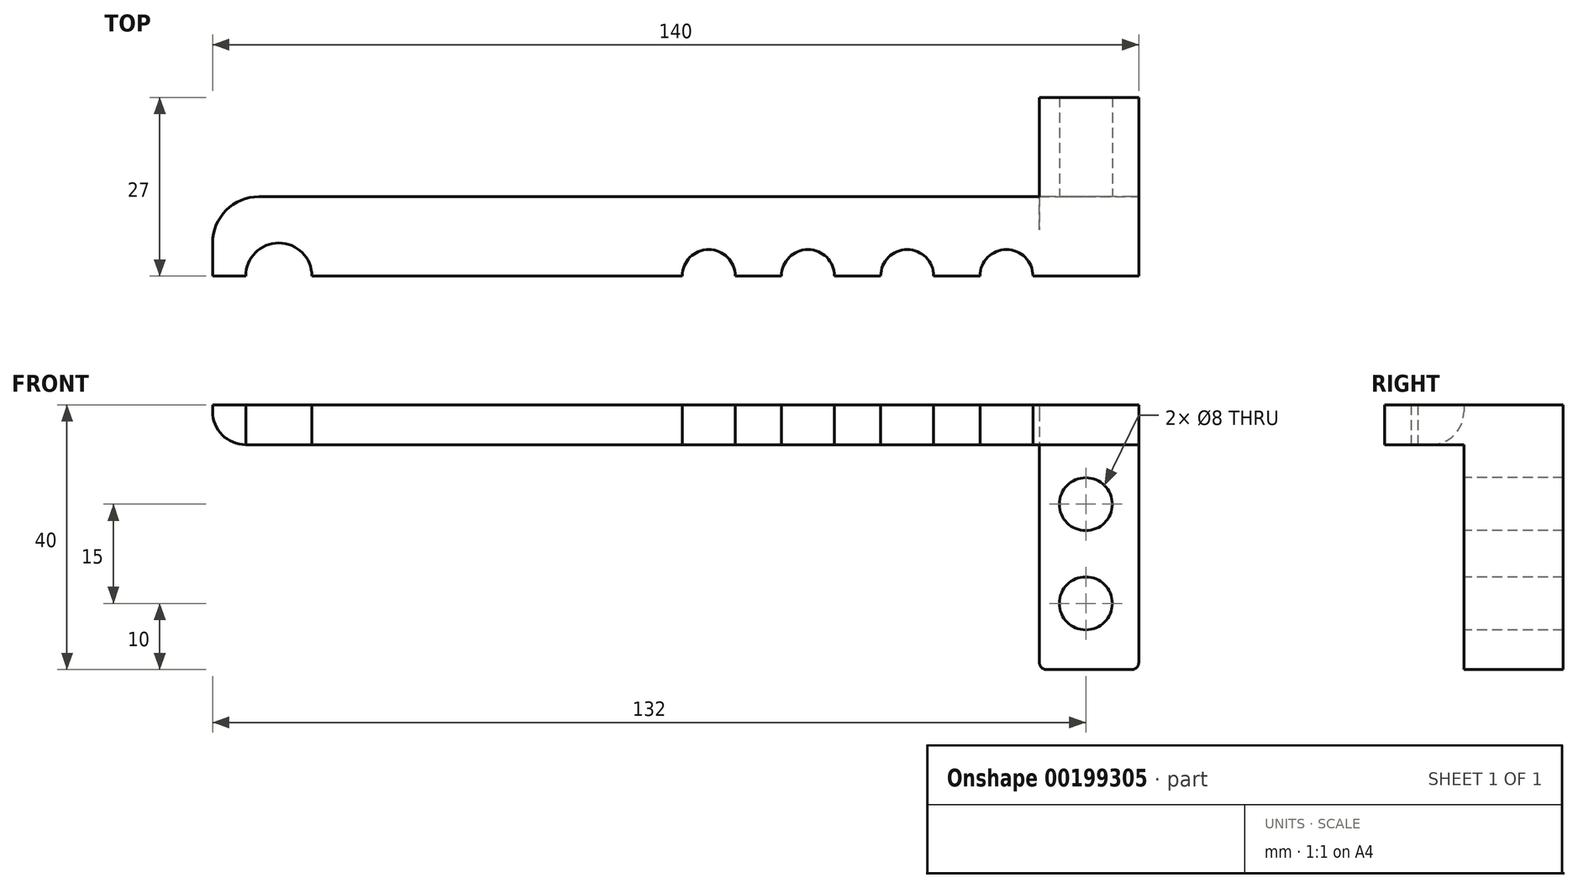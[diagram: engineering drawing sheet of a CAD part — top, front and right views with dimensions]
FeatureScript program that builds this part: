
annotation { "Feature Type Name" : "Feature", "Feature Type Description" : "" }
export const myFeature = defineFeature(function(context is Context, id is Id, definition is map)
    precondition{}
    {
        {
            var Q0;
            Q0=qCreatedBy(makeId("Top.planeOp"),FACE);
            var sketch = newSketch(context, id + "F0", { "sketchPlane" : qUnion([Q0])});
            skCircle(sketch, "E0", {"center": v(-65, 0) * mm, "radius": 5 * mm});
            skCircle(sketch, "E1", {"center": v(0, 0) * mm, "radius": 4 * mm});
            skCircle(sketch, "E2", {"center": v(15, 0) * mm, "radius": 4 * mm});
            skCircle(sketch, "E3", {"center": v(30, 0) * mm, "radius": 4 * mm});
            skCircle(sketch, "E4", {"center": v(45, 0) * mm, "radius": 4 * mm});
            skLineSegment(sketch, "E5", {"start": v(-75, 0) * mm, "end": v(-75, 12) * mm});
            skLineSegment(sketch, "E6", {"start": v(-75, 12) * mm, "end": v(65, 12) * mm});
            skLineSegment(sketch, "E7", {"start": v(65, 12) * mm, "end": v(65, 0) * mm});
            skLineSegment(sketch, "E8", {"start": v(65, 0) * mm, "end": v(-75, 0) * mm});
            skSolve(sketch);
        }
        {
            var Q0;
            {var subQ11=sQuery(id+"F0.wireOp",EDGE,"E5");Q0=makeQuery(id+"F0.imprint","IMPRINT",FACE,{"disambiguationData":[TD([[makeQuery(id+"F0.imprint","IMPRINT",EDGE,{"derivedFrom":subQ11}),-1.0]])]});}
            extrude(context, id + "F1", {"entities" : qUnion([Q0]), "depth" : 6 * mm});
        }
        {
            var Q0;
            Q0=makeQuery(id+"F1.opExtrude","SWEPT_EDGE",EDGE,{"disambiguationData":[OSD([sQuery(id+"F0.wireOp",EDGE,"E5"),sQuery(id+"F0.wireOp",EDGE,"E6")])]});
            fillet(context, id + "F2", {"entities" : qUnion([Q0]), "radius" : 7 * mm, "tangentPropagation" : true, "allowEdgeOverflow" : false});
        }
        {
            var Q0;
            Q0=makeQuery(id+"F1.opExtrude","SWEPT_FACE",FACE,{"disambiguationData":[OSD([sQuery(id+"F0.wireOp",EDGE,"E6")])]});
            var sketch = newSketch(context, id + "F3", { "sketchPlane" : qUnion([Q0])});
            skLineSegment(sketch, "E9.bottom", {"start": v(-65, 6) * mm, "end": v(-50, 6) * mm});
            skLineSegment(sketch, "E9.top", {"start": v(-65, -34) * mm, "end": v(-50, -34) * mm});
            skLineSegment(sketch, "E9.left", {"start": v(-65, 6) * mm, "end": v(-65, -34) * mm});
            skLineSegment(sketch, "E9.right", {"start": v(-50, 6) * mm, "end": v(-50, -34) * mm});
            skSolve(sketch);
        }
        {
            var Q0;
            {var subQ0=sQuery(id+"F3.wireOp",EDGE,"E9.top");Q0=makeQuery(id+"F3.imprint","IMPRINT",FACE,{"disambiguationData":[TD([[makeQuery(id+"F3.imprint","IMPRINT",EDGE,{"derivedFrom":subQ0}),1.0]])]});}
            var Q1;
            {var subQ0=sQuery(id+"F3.wireOp",EDGE,"E9.bottom");Q1=makeQuery(id+"F3.imprint","IMPRINT",FACE,{"disambiguationData":[TD([[makeQuery(id+"F3.imprint","IMPRINT",EDGE,{"derivedFrom":subQ0}),1.0]])]});}
            extrude(context, id + "F4", {"entities" : qUnion([Q0, Q1]), "operationType" : NewBodyOperationType.ADD, "depth" : 15 * mm});
        }
        {
            var Q0;
            Q0=makeQuery(id+"F4.opExtrude","CAP_FACE",FACE,{"disambiguationData":[OSD([sQuery(id+"F3.wireOp",EDGE,"E9.bottom"),sQuery(id+"F3.wireOp",EDGE,"E9.top"),sQuery(id+"F3.wireOp",EDGE,"E9.left"),sQuery(id+"F3.wireOp",EDGE,"E9.right")])],"isStart":true});
            var sketch = newSketch(context, id + "F5", { "sketchPlane" : qUnion([Q0])});
            skCircle(sketch, "E10", {"center": v(57, -9) * mm, "radius": 4 * mm});
            skCircle(sketch, "E11", {"center": v(57, -24) * mm, "radius": 4 * mm});
            skSolve(sketch);
        }
        {
            var Q0;
            Q0=makeQuery(id+"F5.imprint","IMPRINT",FACE,{"disambiguationData":[TD([[makeQuery(id+"F5.imprint","IMPRINT",EDGE,{"derivedFrom":sQuery(id+"F5.wireOp",EDGE,"E10")}),1.0]])]});
            var Q1;
            Q1=makeQuery(id+"F5.imprint","IMPRINT",FACE,{"disambiguationData":[TD([[makeQuery(id+"F5.imprint","IMPRINT",EDGE,{"derivedFrom":sQuery(id+"F5.wireOp",EDGE,"E11")}),1.0]])]});
            extrude(context, id + "F6", {"entities" : qUnion([Q0, Q1]), "operationType" : NewBodyOperationType.REMOVE, "oppositeDirection" : true, "depth" : 25 * mm});
        }
        {
            var Q0;
            {var subQ2=sQuery(id+"F0.wireOp",EDGE,"E7");var subQ3=sQuery(id+"F0.wireOp",EDGE,"E6");Q0=makeQuery(id+"F4.boolean.opBoolean","SPLIT",EDGE,{"disambiguationData":[TD([makeQuery(id+"F1.opExtrude","SWEPT_FACE",FACE,{"disambiguationData":[OSD([subQ2])]})])],"derivedFrom":makeQuery(id+"F1.opExtrude","CAP_EDGE",EDGE,{"disambiguationData":[OSD([subQ3])],"isStart":true})});}
            fillet(context, id + "F7", {"entities" : qUnion([Q0]), "radius" : 5 * mm, "tangentPropagation" : true, "allowEdgeOverflow" : false});
        }
        {
            var Q0;
            Q0=makeQuery(id+"F4.opExtrude","SWEPT_EDGE",EDGE,{"disambiguationData":[OSD([sQuery(id+"F3.wireOp",EDGE,"E9.top"),sQuery(id+"F3.wireOp",EDGE,"E9.left")])]});
            var Q1;
            Q1=makeQuery(id+"F4.opExtrude","SWEPT_EDGE",EDGE,{"disambiguationData":[OSD([sQuery(id+"F3.wireOp",EDGE,"E9.top"),sQuery(id+"F3.wireOp",EDGE,"E9.right")])]});
            fillet(context, id + "F8", {"entities" : qUnion([Q0, Q1]), "radius" : 1 * mm, "tangentPropagation" : true, "allowEdgeOverflow" : false});
        }
    });
